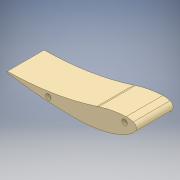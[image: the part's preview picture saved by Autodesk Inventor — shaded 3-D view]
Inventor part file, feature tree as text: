
AUTODESK INVENTOR PART (.ipt)
format: ipt  version: 2018 (Build 220112000, 112)  size: 112,640 bytes
history: native  units: mm
features: extrude x1, sketch x1, projected_geometry x1
ambient origin geometry x8: Origin, YZ Plane, XZ Plane, XY Plane, X Axis, Y Axis, Z Axis, Center Point
bodies: Body1 (feature_tree)
feature tree (3):
  extrude  "押し出し1"  Depth=41.5mm TaperAngle=0.0deg
  sketch  "スケッチ1"
  projected_geometry  "投影ループ1"
